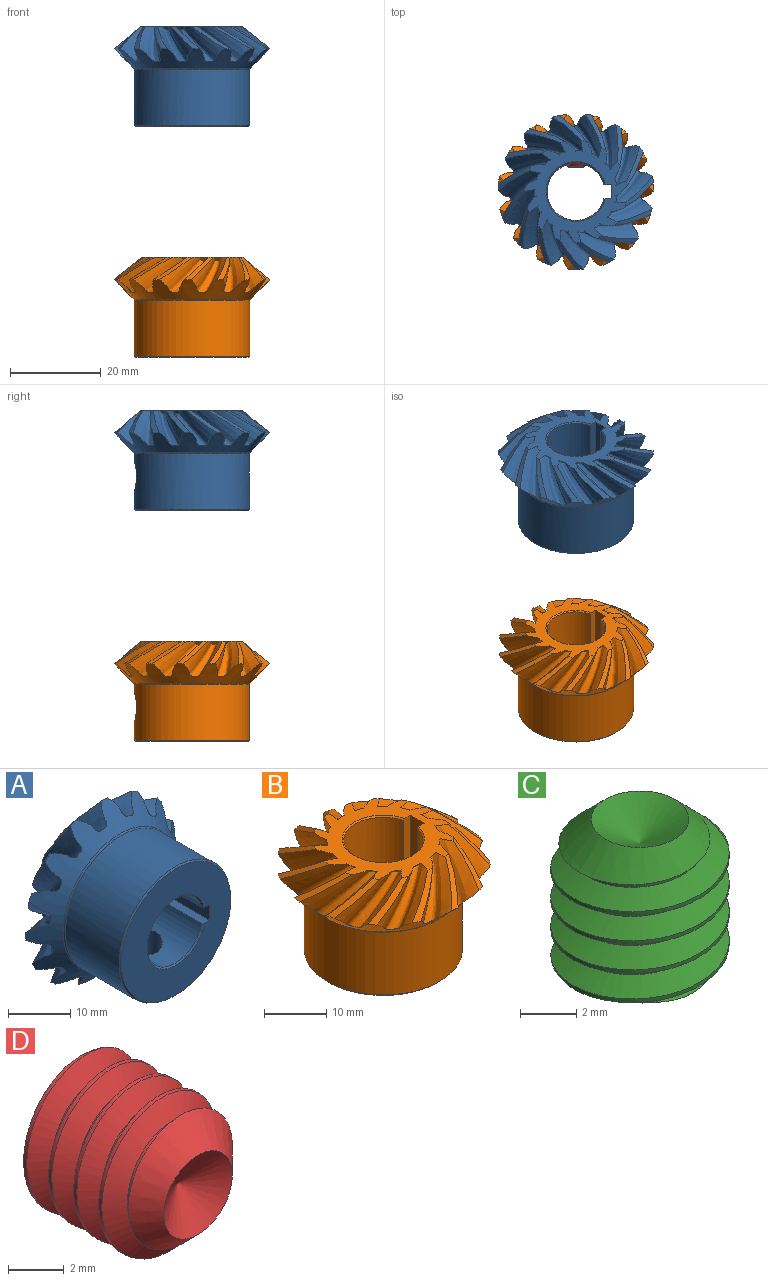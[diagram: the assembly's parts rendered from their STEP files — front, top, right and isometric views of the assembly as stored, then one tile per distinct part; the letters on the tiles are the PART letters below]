
ASSEMBLY  parts=4 mates=2
PART A: 59 faces, bbox 35.8x23.3x35.9 mm
  f0: cylinder r=12.7mm len=25.4mm, axis (0,1,0), area 935mm2, adj f50,f57,f58
  f1: cylinder r=6.35mm len=21.5mm, axis (0,1,0), area 756.1mm2, adj f51,f52,f54,f55,f56
  f2: plane 22.56x22.55mm, normal (0,1,0), area 176.1mm2, adj f4,f5,f6,f7,f8,f9,f10,f11
  f3: plane 24.89x24.89mm, normal (0,-1,0), area 345.8mm2, adj f50,f52,f53,f54,f55
  f4: cone r=17.15mm half-angle=50.6deg, axis (0,-1,0), area 10.2mm2, adj f2,f18,f47,f49
  f5: cone r=17.15mm half-angle=50.6deg, axis (0,-1,0), area 10.2mm2, adj f2,f18,f45,f47
  f6: cone r=17.15mm half-angle=50.6deg, axis (0,-1,0), area 10.2mm2, adj f2,f18,f43,f45
  f7: cone r=17.15mm half-angle=50.6deg, axis (0,-1,0), area 10.2mm2, adj f2,f18,f41,f43
  f8: cone r=17.15mm half-angle=50.6deg, axis (0,-1,0), area 10.2mm2, adj f2,f18,f39,f41
  f9: cone r=17.15mm half-angle=50.6deg, axis (0,-1,0), area 10.2mm2, adj f2,f18,f37,f39
  f10: cone r=17.15mm half-angle=50.6deg, axis (0,-1,0), area 10.2mm2, adj f2,f18,f35,f37
  f11: cone r=17.15mm half-angle=50.6deg, axis (0,-1,0), area 10.2mm2, adj f2,f18,f33,f35
  f12: cone r=17.15mm half-angle=50.6deg, axis (0,-1,0), area 10.2mm2, adj f2,f18,f31,f33
  f13: cone r=17.15mm half-angle=50.6deg, axis (0,-1,0), area 10.2mm2, adj f2,f18,f29,f31
  f14: cone r=17.15mm half-angle=50.6deg, axis (0,-1,0), area 10.2mm2, adj f2,f18,f27,f29
  f15: cone r=17.15mm half-angle=50.6deg, axis (0,-1,0), area 10.2mm2, adj f2,f18,f25,f27
  f16: cone r=17.15mm half-angle=50.6deg, axis (0,-1,0), area 10.2mm2, adj f2,f18,f23,f25
  f17: cone r=17.15mm half-angle=50.6deg, axis (0,-1,0), area 10.2mm2, adj f2,f18,f21,f23
  f18: cone r=12.7mm half-angle=45deg, axis (0,1,0), area 367.4mm2, adj f4,f5,f6,f7,f8,f9,f10,f11
  f19: cone r=17.15mm half-angle=50.6deg, axis (0,-1,0), area 10.2mm2, adj f2,f18,f21,f49
  f20: plane 1.54x1.12mm, normal (0.33,-0.71,-0.62), area 1.1mm2, adj f2,f21
  f21: bspline ~11.06x10.53mm, area 80.6mm2, adj f2,f17,f18,f19,f20
  f22: plane 1.45x1.27mm, normal (0.56,-0.71,-0.43), area 1.1mm2, adj f2,f23
  f23: bspline ~12.91x9.23mm, area 80.6mm2, adj f2,f16,f17,f18,f22
  f24: plane 1.62x0.87mm, normal (0.69,-0.71,-0.17), area 1.1mm2, adj f2,f25
  f25: bspline ~14.37x9.23mm, area 80.6mm2, adj f2,f15,f16,f18,f24
  f26: plane 1.64x0.81mm, normal (0.7,-0.71,0.12), area 1.1mm2, adj f2,f27
  f27: bspline ~13.36x9.25mm, area 80.6mm2, adj f2,f14,f15,f18,f26
  f28: plane 1.48x1.22mm, normal (0.59,-0.71,0.4), area 1.1mm2, adj f2,f29
  f29: bspline ~10.94x10.04mm, area 80.6mm2, adj f2,f13,f14,f18,f28
  f30: plane 1.51x1.18mm, normal (0.37,-0.71,0.6), area 1.1mm2, adj f2,f31
  f31: bspline ~13.5x9.23mm, area 80.6mm2, adj f2,f12,f13,f18,f30
  f32: plane 1.65x0.76mm, normal (0.1,-0.71,0.7), area 1.1mm2, adj f2,f33
  f33: bspline ~14.35x9.23mm, area 80.6mm2, adj f2,f11,f12,f18,f32
  f34: plane 1.61x0.91mm, normal (-0.2,-0.71,0.68), area 1.1mm2, adj f2,f35
  f35: bspline ~12.73x9.78mm, area 80.6mm2, adj f2,f10,f11,f18,f34
  f36: plane 1.42x1.3mm, normal (-0.46,-0.71,0.54), area 1.1mm2, adj f2,f37
  f37: bspline ~11.72x9.23mm, area 80.6mm2, adj f2,f9,f10,f18,f36
  f38: plane 1.56x1.08mm, normal (-0.64,-0.71,0.31), area 1.1mm2, adj f2,f39
  f39: bspline ~13.94x9.23mm, area 80.6mm2, adj f2,f8,f9,f18,f38
  f40: plane 1.67x0.65mm, normal (-0.71,-0.71,0.02), area 1.1mm2, adj f2,f41
  f41: bspline ~14.18x9.23mm, area 80.6mm2, adj f2,f7,f8,f18,f40
  f42: plane 1.58x1.02mm, normal (-0.65,-0.71,-0.27), area 1.1mm2, adj f2,f43
  f43: bspline ~11.96x10.21mm, area 80.6mm2, adj f2,f6,f7,f18,f42
  f44: plane 1.38x1.35mm, normal (-0.49,-0.71,-0.51), area 1.1mm2, adj f2,f45
  f45: bspline ~12.38x9.23mm, area 80.6mm2, adj f2,f5,f6,f18,f44
  f46: plane 1.59x0.98mm, normal (-0.24,-0.71,-0.67), area 1.1mm2, adj f2,f47
  f47: bspline ~14.24x9.23mm, area 80.6mm2, adj f2,f4,f5,f18,f46
  f48: plane 1.66x0.7mm, normal (0.05,-0.71,-0.71), area 1.1mm2, adj f2,f49
  f49: bspline ~13.85x9.23mm, area 80.6mm2, adj f2,f4,f18,f19,f48
  f50: cone r=12.45mm half-angle=45deg, axis (0,1,0), area 28.4mm2, adj f0,f3
  f51: cone r=6.35mm half-angle=45deg, axis (0,1,0), area 13.5mm2, adj f1,f2,f54,f55
  f52: cone r=6.6mm half-angle=45deg, axis (0,-1,0), area 13.5mm2, adj f1,f3,f54,f55
  f53: plane 22.01x3.18mm, normal (-1,0,0), area 69.9mm2, adj f2,f3,f54,f55
  f54: plane 22.01x1.59mm, normal (0,0,-1), area 34.9mm2, adj f1,f2,f3,f51,f52,f53
  f55: plane 22.01x1.59mm, normal (0,0,1), area 34.9mm2, adj f1,f2,f3,f51,f52,f53
  f56: cylinder r=3.17mm len=6.35mm, axis (0,0,-1), area 120.8mm2, adj f1,f57
  f57: bspline ~7.31x7.13mm, area 11.3mm2, adj f0,f56
  f58: torus R=13.21mm, axis (0,1,0), area 32mm2, adj f0,f18
PART B: 59 faces, bbox 35.8x35.9x23.3 mm
  f0: cylinder r=12.7mm len=25.4mm, axis (0,0,1), area 943.4mm2, adj f50,f56,f58
  f1: cylinder r=6.35mm len=21.5mm, axis (0,0,1), area 756.1mm2, adj f51,f52,f54,f55,f57
  f2: plane 22.55x22.54mm, normal (0,0,1), area 176.1mm2, adj f4,f5,f6,f7,f8,f9,f10,f11
  f3: plane 24.89x24.89mm, normal (0,0,-1), area 345.8mm2, adj f50,f52,f53,f54,f55
  f4: cone r=17.15mm half-angle=50.6deg, axis (0,0,-1), area 10.2mm2, adj f2,f18,f47,f49
  f5: cone r=17.15mm half-angle=50.6deg, axis (0,0,-1), area 10.2mm2, adj f2,f18,f45,f47
  f6: cone r=17.15mm half-angle=50.6deg, axis (0,0,-1), area 10.2mm2, adj f2,f18,f43,f45
  f7: cone r=17.15mm half-angle=50.6deg, axis (0,0,-1), area 10.2mm2, adj f2,f18,f41,f43
  f8: cone r=17.15mm half-angle=50.6deg, axis (0,0,-1), area 10.2mm2, adj f2,f18,f39,f41
  f9: cone r=17.15mm half-angle=50.6deg, axis (0,0,-1), area 10.2mm2, adj f2,f18,f37,f39
  f10: cone r=17.15mm half-angle=50.6deg, axis (0,0,-1), area 10.2mm2, adj f2,f18,f35,f37
  f11: cone r=17.15mm half-angle=50.6deg, axis (0,0,-1), area 10.2mm2, adj f2,f18,f33,f35
  f12: cone r=17.15mm half-angle=50.6deg, axis (0,0,-1), area 10.2mm2, adj f2,f18,f31,f33
  f13: cone r=17.15mm half-angle=50.6deg, axis (0,0,-1), area 10.2mm2, adj f2,f18,f29,f31
  f14: cone r=17.15mm half-angle=50.6deg, axis (0,0,-1), area 10.2mm2, adj f2,f18,f27,f29
  f15: cone r=17.15mm half-angle=50.6deg, axis (0,0,-1), area 10.2mm2, adj f2,f18,f25,f27
  f16: cone r=17.15mm half-angle=50.6deg, axis (0,0,-1), area 10.2mm2, adj f2,f18,f23,f25
  f17: cone r=17.15mm half-angle=50.6deg, axis (0,0,-1), area 10.2mm2, adj f2,f18,f21,f23
  f18: cone r=12.7mm half-angle=45deg, axis (0,0,1), area 377.6mm2, adj f4,f5,f6,f7,f8,f9,f10,f11
  f19: cone r=17.15mm half-angle=50.6deg, axis (0,0,-1), area 10.2mm2, adj f2,f18,f21,f49
  f20: plane 1.54x1.12mm, normal (-0.33,0.62,-0.71), area 1.1mm2, adj f2,f21
  f21: bspline ~11.06x10.53mm, area 80.6mm2, adj f2,f17,f18,f19,f20
  f22: plane 1.66x0.7mm, normal (-0.05,0.71,-0.71), area 1.1mm2, adj f2,f23
  f23: bspline ~13.85x9.23mm, area 80.6mm2, adj f2,f16,f17,f18,f22
  f24: plane 1.59x0.98mm, normal (0.24,0.67,-0.71), area 1.1mm2, adj f2,f25
  f25: bspline ~14.24x9.23mm, area 80.6mm2, adj f2,f15,f16,f18,f24
  f26: plane 1.38x1.35mm, normal (0.49,0.51,-0.71), area 1.1mm2, adj f2,f27
  f27: bspline ~12.38x9.23mm, area 80.6mm2, adj f2,f14,f15,f18,f26
  f28: plane 1.58x1.02mm, normal (0.65,0.27,-0.71), area 1.1mm2, adj f2,f29
  f29: bspline ~11.96x10.21mm, area 80.7mm2, adj f2,f13,f14,f18,f28
  f30: plane 1.67x0.66mm, normal (0.71,-0.02,-0.71), area 1.1mm2, adj f2,f31
  f31: bspline ~14.18x9.23mm, area 80.6mm2, adj f2,f12,f13,f18,f30
  f32: plane 1.56x1.09mm, normal (0.64,-0.31,-0.71), area 1.1mm2, adj f2,f33
  f33: bspline ~13.94x9.23mm, area 80.6mm2, adj f2,f11,f12,f18,f32
  f34: plane 1.43x1.3mm, normal (0.46,-0.54,-0.71), area 1.1mm2, adj f2,f35
  f35: bspline ~11.72x9.23mm, area 80.6mm2, adj f2,f10,f11,f18,f34
  f36: plane 1.61x0.91mm, normal (0.2,-0.68,-0.71), area 1.1mm2, adj f2,f37
  f37: bspline ~12.73x9.78mm, area 80.6mm2, adj f2,f9,f10,f18,f36
  f38: plane 1.65x0.77mm, normal (-0.1,-0.7,-0.71), area 1.1mm2, adj f2,f39
  f39: bspline ~14.35x9.23mm, area 80.6mm2, adj f2,f8,f9,f18,f38
  f40: plane 1.51x1.18mm, normal (-0.37,-0.6,-0.71), area 1.1mm2, adj f2,f41
  f41: bspline ~13.5x9.23mm, area 80.6mm2, adj f2,f7,f8,f18,f40
  f42: plane 1.49x1.22mm, normal (-0.59,-0.4,-0.71), area 1.1mm2, adj f2,f43
  f43: bspline ~10.94x10.04mm, area 80.6mm2, adj f2,f6,f7,f18,f42
  f44: plane 1.64x0.81mm, normal (-0.7,-0.12,-0.71), area 1.1mm2, adj f2,f45
  f45: bspline ~13.36x9.25mm, area 80.6mm2, adj f2,f5,f6,f18,f44
  f46: plane 1.62x0.88mm, normal (-0.69,0.17,-0.71), area 1.1mm2, adj f2,f47
  f47: bspline ~14.37x9.23mm, area 80.6mm2, adj f2,f4,f5,f18,f46
  f48: plane 1.45x1.27mm, normal (-0.56,0.43,-0.71), area 1.1mm2, adj f2,f49
  f49: bspline ~12.91x9.23mm, area 80.6mm2, adj f2,f4,f18,f19,f48
  f50: cone r=12.45mm half-angle=45deg, axis (0,0,1), area 28.4mm2, adj f0,f3
  f51: cone r=6.35mm half-angle=45deg, axis (0,0,1), area 13.5mm2, adj f1,f2,f54,f55
  f52: cone r=6.6mm half-angle=45deg, axis (0,0,-1), area 13.5mm2, adj f1,f3,f54,f55
  f53: plane 22.01x3.18mm, normal (-1,0,0), area 69.9mm2, adj f2,f3,f54,f55
  f54: plane 22.01x1.59mm, normal (0,1,0), area 34.9mm2, adj f1,f2,f3,f51,f52,f53
  f55: plane 22.01x1.59mm, normal (0,-1,0), area 34.9mm2, adj f1,f2,f3,f51,f52,f53
  f56: torus R=12.95mm, axis (0,0,1), area 16mm2, adj f0,f18
  f57: cylinder r=3.17mm len=6.35mm, axis (0,1,0), area 120.8mm2, adj f1,f58
  f58: bspline ~7.31x7.14mm, area 11.3mm2, adj f0,f57
PART C: 27 faces, bbox 7.3x7.3x7.5 mm
  f0: plane 1.26x0.97mm, normal (0,0,-1), area 0.1mm2, adj f1,f25,f26
  f1: plane 2.68x2.39mm, normal (-0.92,0.38,0), area 3.3mm2, adj f0,f2,f3,f24,f26
  f2: plane 1.57x0.56mm, normal (0,0,-1), area 0.1mm2, adj f1,f24,f25
  f3: cone r=1.83mm half-angle=45deg, axis (0,0,-1), area 0mm2, adj f1,f4
  f4: plane 5.75x5.63mm, normal (0,0,-1), area 9.1mm2, adj f3,f5,f9,f10,f11,f12,f13,f21
  f5: bspline ~6.19x4.92mm, area 10.6mm2, adj f4,f6,f9,f11
  f6: cone r=1.74mm half-angle=45deg, axis (0,0,-1), area 20.8mm2, adj f5,f7,f8,f9,f11
  f7: cylinder r=3.17mm len=6.35mm, axis (0,0,-1), area 11.1mm2, adj f6,f9,f10,f11
  f8: cone r=0mm half-angle=59deg, axis (0,0,1), area 11.1mm2, adj f6
  f9: bspline ~6.64x6.64mm, area 66.8mm2, adj f4,f5,f6,f7,f10
  f10: cone r=3.17mm half-angle=55deg, axis (0,0,1), area 5.6mm2, adj f4,f7,f9,f11
  f11: bspline ~6.64x6.64mm, area 69mm2, adj f4,f5,f6,f7,f10
  f12: cone r=1.83mm half-angle=45deg, axis (0,0,-1), area 0mm2, adj f4,f26
  f13: cone r=1.83mm half-angle=45deg, axis (0,0,-1), area 0mm2, adj f4,f14
  f14: plane 2.68x2.15mm, normal (0.79,0.61,0), area 3.3mm2, adj f13,f15,f16,f17,f26
  f15: plane 1.47x0.73mm, normal (0,0,-1), area 0.1mm2, adj f14,f25,f26
  f16: plane 1.57x0.56mm, normal (0,0,-1), area 0.1mm2, adj f14,f17,f25
  f17: plane 2.68x2.39mm, normal (0.92,-0.38,0), area 3.3mm2, adj f14,f16,f18,f19,f21
  f18: plane 1.26x0.97mm, normal (0,0,-1), area 0.1mm2, adj f17,f19,f25
  f19: plane 2.68x2.51mm, normal (0.13,-0.99,0), area 3.3mm2, adj f17,f18,f20,f22,f24
  f20: plane 1.47x0.73mm, normal (0,0,-1), area 0.1mm2, adj f19,f24,f25
  f21: cone r=1.83mm half-angle=45deg, axis (0,0,-1), area 0mm2, adj f4,f17
  f22: cone r=1.83mm half-angle=45deg, axis (0,0,-1), area 0mm2, adj f4,f19
  f23: cone r=1.83mm half-angle=45deg, axis (0,0,-1), area 0mm2, adj f4,f24
  f24: plane 2.68x2.15mm, normal (-0.79,-0.61,0), area 3.3mm2, adj f1,f2,f19,f20,f23
  f25: cone r=1.59mm half-angle=60deg, axis (0,0,-1), area 9.1mm2, adj f0,f2,f15,f16,f18,f20
  f26: plane 2.68x2.51mm, normal (-0.13,0.99,0), area 3.3mm2, adj f0,f1,f12,f14,f15
PART D: 27 faces, bbox 7.5x7.5x7.5 mm
  f0: plane 1.38x0.79mm, normal (0,1,0), area 0.1mm2, adj f1,f25,f26
  f1: plane 2.68x2.53mm, normal (0,0,1), area 3.3mm2, adj f0,f2,f3,f24,f26
  f2: plane 1.37x0.8mm, normal (0,1,0), area 0.1mm2, adj f1,f24,f25
  f3: cone r=1.83mm half-angle=45deg, axis (0,1,0), area 0mm2, adj f1,f4
  f4: plane 5.77x5.7mm, normal (0,1,0), area 9.1mm2, adj f3,f5,f9,f10,f11,f12,f13,f21
  f5: bspline ~6.19x5.04mm, area 10.6mm2, adj f4,f6,f9,f11
  f6: cone r=1.74mm half-angle=45deg, axis (0,1,0), area 20.8mm2, adj f5,f7,f8,f9,f11
  f7: cylinder r=3.17mm len=6.35mm, axis (0,1,0), area 11.1mm2, adj f6,f9,f10,f11
  f8: cone r=0mm half-angle=59deg, axis (0,-1,0), area 11.1mm2, adj f6
  f9: bspline ~6.81x6.81mm, area 66.8mm2, adj f4,f5,f6,f7,f10
  f10: cone r=3.17mm half-angle=55deg, axis (0,-1,0), area 5.6mm2, adj f4,f7,f9,f11
  f11: bspline ~6.81x6.81mm, area 69mm2, adj f4,f5,f6,f7,f10
  f12: cone r=1.83mm half-angle=45deg, axis (0,1,0), area 0mm2, adj f4,f26
  f13: cone r=1.83mm half-angle=45deg, axis (0,1,0), area 0mm2, adj f4,f14
  f14: plane 2.68x2.29mm, normal (0.87,0,-0.5), area 3.3mm2, adj f13,f15,f16,f17,f26
  f15: plane 1.59x0.46mm, normal (0,1,0), area 0.1mm2, adj f14,f25,f26
  f16: plane 1.37x0.8mm, normal (0,1,0), area 0.1mm2, adj f14,f17,f25
  f17: plane 2.68x2.53mm, normal (0,0,-1), area 3.3mm2, adj f14,f16,f18,f19,f21
  f18: plane 1.38x0.79mm, normal (0,1,0), area 0.1mm2, adj f17,f19,f25
  f19: plane 2.68x2.28mm, normal (-0.86,0,-0.5), area 3.3mm2, adj f17,f18,f20,f22,f24
  f20: plane 1.59x0.46mm, normal (0,1,0), area 0.1mm2, adj f19,f24,f25
  f21: cone r=1.83mm half-angle=45deg, axis (0,1,0), area 0mm2, adj f4,f17
  f22: cone r=1.83mm half-angle=45deg, axis (0,1,0), area 0mm2, adj f4,f19
  f23: cone r=1.83mm half-angle=45deg, axis (0,1,0), area 0mm2, adj f4,f24
  f24: plane 2.68x2.29mm, normal (-0.87,0,0.5), area 3.3mm2, adj f1,f2,f19,f20,f23
  f25: cone r=1.59mm half-angle=60deg, axis (0,1,0), area 9.1mm2, adj f0,f2,f15,f16,f18,f20
  f26: plane 2.68x2.28mm, normal (0.86,0,0.5), area 3.3mm2, adj f0,f1,f12,f14,f15
PLACE A rot(axis=(1,0,0),90deg) t=(-4.7,-7.52,49.26)mm
PLACE B t=(-4.7,-16.2,7.13)mm
PLACE C rot(axis=(1,0,0),90deg) t=(-4.7,-8.26,-1.54)mm
PLACE D t=(-4.7,-17.04,57.93)mm
MATE fastened C.f6 <-> B.f57  axis (0,1,0) through (3.97,-2.07,-17)mm
MATE fastened D.f3 <-> A.f56  axis (0,-1,0) through (3.97,-2.07,33.8)mm
